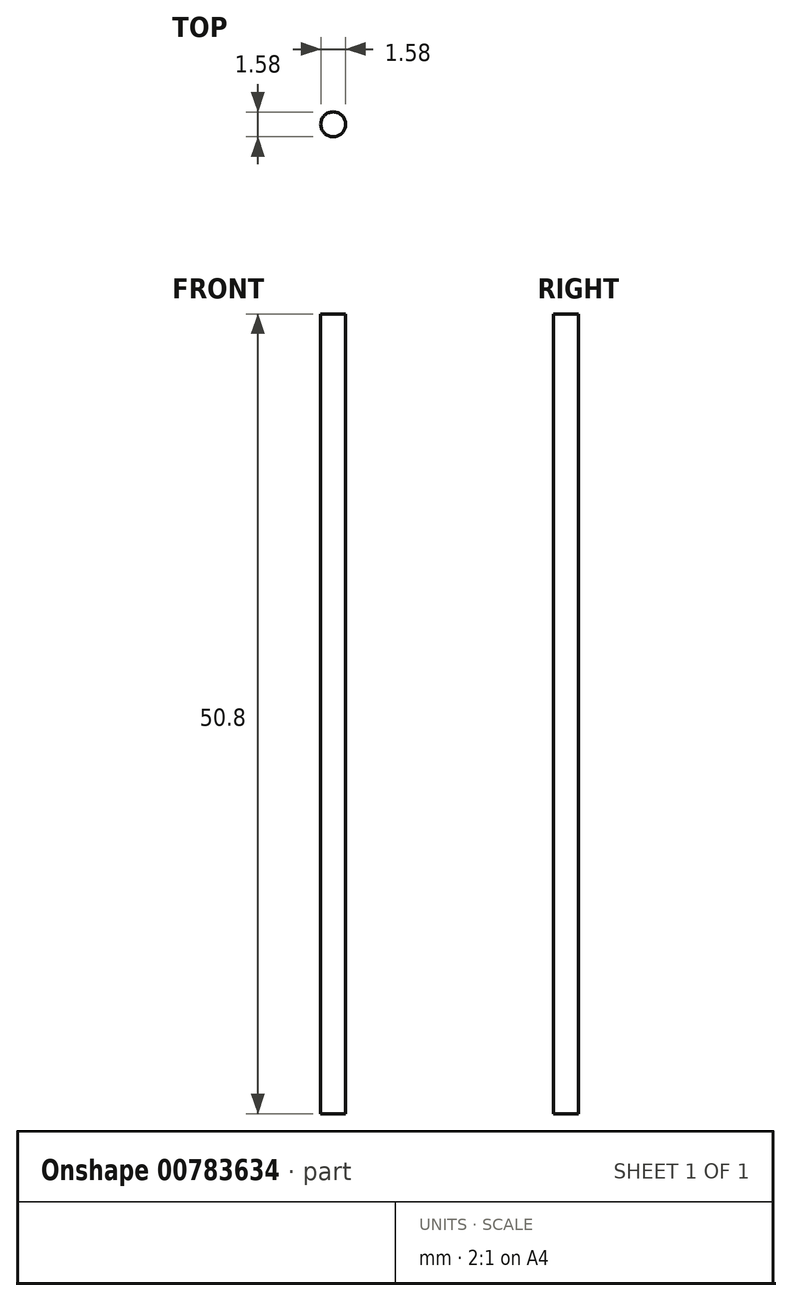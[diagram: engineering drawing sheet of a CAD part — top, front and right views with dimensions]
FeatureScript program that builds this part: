
annotation { "Feature Type Name" : "Feature", "Feature Type Description" : "" }
export const myFeature = defineFeature(function(context is Context, id is Id, definition is map)
    precondition{}
    {
        {
            var Q0;
            Q0=qCreatedBy(makeId("Front.planeOp"),FACE);
            var sketch = newSketch(context, id + "F0", { "sketchPlane" : qUnion([Q0])});
            skLineSegment(sketch, "E0.bottom", {"start": v(-0.8, 46.28) * mm, "end": v(0, 46.28) * mm});
            skLineSegment(sketch, "E0.top", {"start": v(-0.8, -4.52) * mm, "end": v(0, -4.52) * mm});
            skLineSegment(sketch, "E0.left", {"start": v(-0.8, 46.28) * mm, "end": v(-0.8, -4.52) * mm});
            skLineSegment(sketch, "E0.right", {"start": v(0, 46.28) * mm, "end": v(0, -4.52) * mm});
            skSolve(sketch);
        }
        {
            var Q0;
            Q0=makeQuery(id+"F0.imprint","IMPRINT",FACE,{"disambiguationData":[TD([[makeQuery(id+"F0.imprint","IMPRINT",EDGE,{"derivedFrom":sQuery(id+"F0.wireOp",EDGE,"E0.bottom")}),-1.0]])]});
            var Q1;
            Q1=sQuery(id+"F0.wireOp",EDGE,"E0.right");
            revolve(context, id + "F1", {"surfaceOperationType" : NewSurfaceOperationType.NEW, "entities" : qUnion([Q0]), "axis" : qUnion([Q1]), "revolveType" : RevolveType.FULL});
        }
    });
